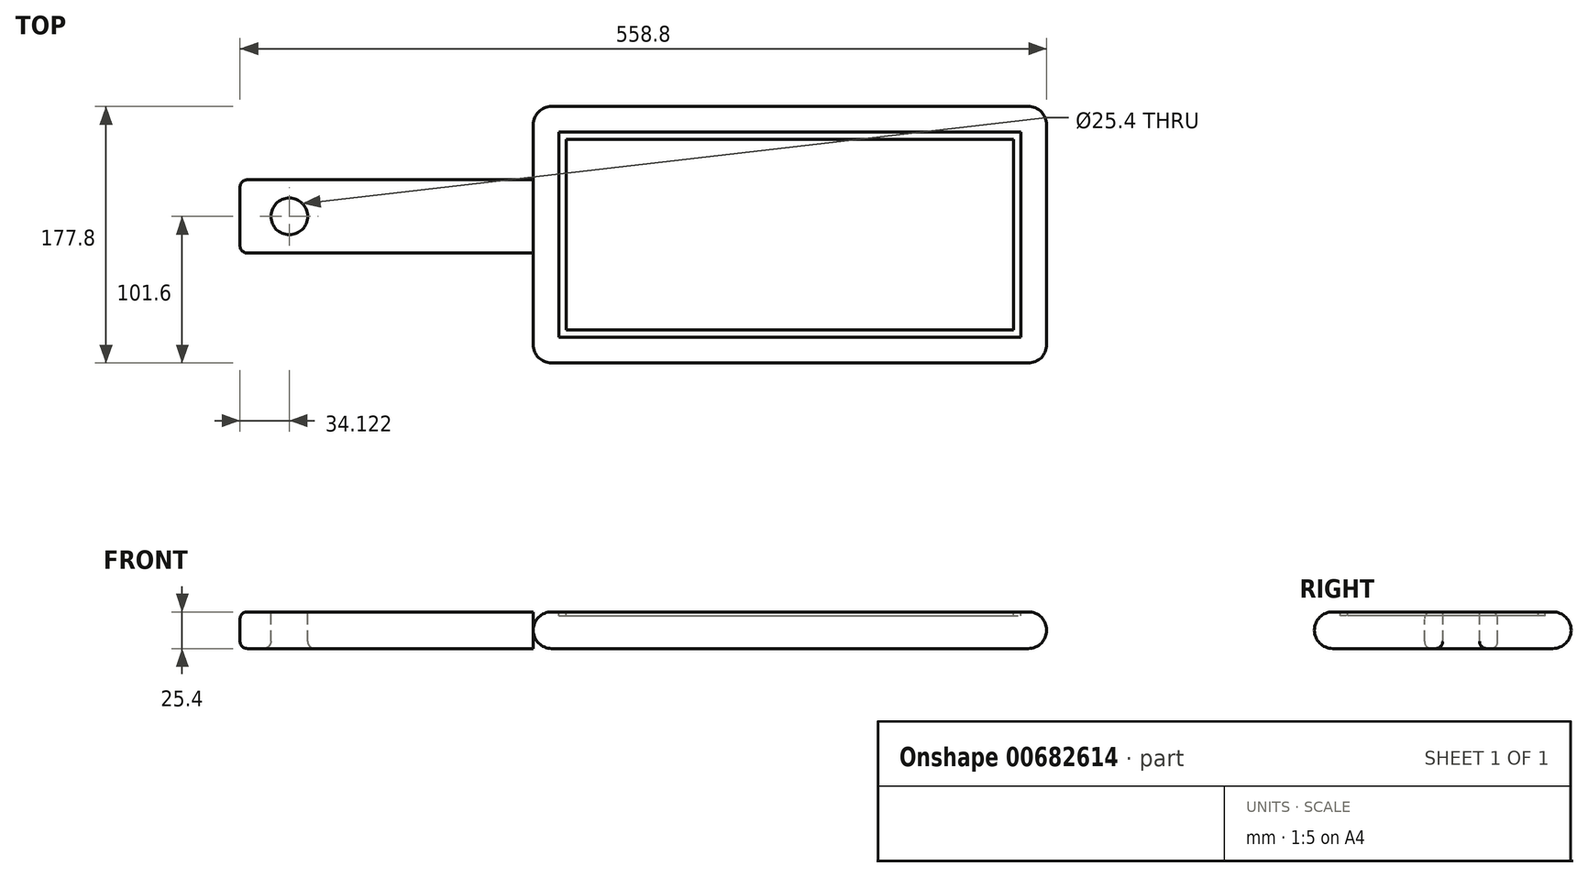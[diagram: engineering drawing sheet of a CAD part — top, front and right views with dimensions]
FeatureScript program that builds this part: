
annotation { "Feature Type Name" : "Feature", "Feature Type Description" : "" }
export const myFeature = defineFeature(function(context is Context, id is Id, definition is map)
    precondition{}
    {
        {
            var Q0;
            Q0=qCreatedBy(makeId("Top.planeOp"),FACE);
            var sketch = newSketch(context, id + "F0", { "sketchPlane" : qUnion([Q0])});
            skLineSegment(sketch, "E0.bottom", {"start": v(0, 0) * mm, "end": v(355.6, 0) * mm});
            skLineSegment(sketch, "E0.top", {"start": v(0, 177.8) * mm, "end": v(355.6, 177.8) * mm});
            skLineSegment(sketch, "E0.left", {"start": v(0, 0) * mm, "end": v(0, 177.8) * mm});
            skLineSegment(sketch, "E0.right", {"start": v(355.6, 0) * mm, "end": v(355.6, 177.8) * mm});
            skSolve(sketch);
        }
        {
            var Q0;
            Q0 = qSketchRegion(id + "F0", true);
            extrude(context, id + "F1", {"entities" : qUnion([Q0]), "depth" : 25.4 * mm, "offsetDistance" : 25.4 * mm});
        }
        {
            var Q0;
            Q0=makeQuery(id+"F1.opExtrude","CAP_FACE",FACE,{"disambiguationData":[OSD([sQuery(id+"F0.wireOp",EDGE,"E0.bottom"),sQuery(id+"F0.wireOp",EDGE,"E0.top"),sQuery(id+"F0.wireOp",EDGE,"E0.left"),sQuery(id+"F0.wireOp",EDGE,"E0.right")])],"isStart":false});
            var sketch = newSketch(context, id + "F2", { "sketchPlane" : qUnion([Q0])});
            skLineSegment(sketch, "E1.bottom", {"start": v(0, 127) * mm, "end": v(-203.2, 127) * mm});
            skLineSegment(sketch, "E1.top", {"start": v(0, 76.2) * mm, "end": v(-203.2, 76.2) * mm});
            skLineSegment(sketch, "E1.left", {"start": v(0, 127) * mm, "end": v(0, 76.2) * mm});
            skLineSegment(sketch, "E1.right", {"start": v(-203.2, 127) * mm, "end": v(-203.2, 76.2) * mm});
            skSolve(sketch);
        }
        {
            var Q0;
            Q0=makeQuery(id+"F2.imprint","IMPRINT",FACE,{"disambiguationData":[TD([[makeQuery(id+"F2.imprint","IMPRINT",EDGE,{"derivedFrom":sQuery(id+"F2.wireOp",EDGE,"E1.bottom")}),1.0]])]});
            extrude(context, id + "F3", {"entities" : qUnion([Q0]), "oppositeDirection" : true, "depth" : 25.4 * mm, "offsetDistance" : 25.4 * mm});
        }
        {
            var Q0;
            Q0=makeQuery(id+"F3.opExtrude","CAP_FACE",FACE,{"disambiguationData":[OSD([sQuery(id+"F2.wireOp",EDGE,"E1.bottom"),sQuery(id+"F2.wireOp",EDGE,"E1.top"),sQuery(id+"F2.wireOp",EDGE,"E1.left"),sQuery(id+"F2.wireOp",EDGE,"E1.right")])],"isStart":true});
            var sketch = newSketch(context, id + "F4", { "sketchPlane" : qUnion([Q0])});
            skCircle(sketch, "E2", {"center": v(-169.08, 101.6) * mm, "radius": 12.7 * mm});
            skSolve(sketch);
        }
        {
            var Q0;
            Q0=makeQuery(id+"F4.imprint","IMPRINT",FACE,{"disambiguationData":[TD([[makeQuery(id+"F4.imprint","IMPRINT",EDGE,{"derivedFrom":sQuery(id+"F4.wireOp",EDGE,"E2")}),1.0]])]});
            extrude(context, id + "F5", {"entities" : qUnion([Q0]), "operationType" : NewBodyOperationType.REMOVE, "endBound" : BoundingType.THROUGH_ALL, "oppositeDirection" : true, "depth" : 25.4 * mm, "offsetDistance" : 25.4 * mm});
        }
        {
            var Q0;
            Q0=makeQuery(id+"F5.boolean.opBoolean","COPY",EDGE,{"derivedFrom":makeQuery(id+"F5.opExtrude","CAP_EDGE",EDGE,{"disambiguationData":[OSD([sQuery(id+"F4.wireOp",EDGE,"E2")])],"isStart":true})});
            var Q1;
            Q1=makeQuery(id+"F5.boolean.opBoolean","INTERSECT",EDGE,{"derivedFrom":[makeQuery(id+"F3.opExtrude","CAP_FACE",FACE,{"disambiguationData":[OSD([sQuery(id+"F2.wireOp",EDGE,"E1.bottom"),sQuery(id+"F2.wireOp",EDGE,"E1.top"),sQuery(id+"F2.wireOp",EDGE,"E1.left"),sQuery(id+"F2.wireOp",EDGE,"E1.right")])],"isStart":false}),makeQuery(id+"F5.opExtrude","SWEPT_FACE",FACE,{"disambiguationData":[OSD([sQuery(id+"F4.wireOp",EDGE,"E2")])]})]});
            var Q2;
            Q2=makeQuery(id+"F3.opExtrude","CAP_EDGE",EDGE,{"disambiguationData":[OSD([sQuery(id+"F2.wireOp",EDGE,"E1.top")])],"isStart":false});
            var Q3;
            Q3=makeQuery(id+"F3.opExtrude","SWEPT_EDGE",EDGE,{"disambiguationData":[OSD([sQuery(id+"F2.wireOp",EDGE,"E1.top"),sQuery(id+"F2.wireOp",EDGE,"E1.right")])]});
            var Q4;
            Q4=makeQuery(id+"F3.opExtrude","CAP_EDGE",EDGE,{"disambiguationData":[OSD([sQuery(id+"F2.wireOp",EDGE,"E1.right")])],"isStart":false});
            var Q5;
            Q5=makeQuery(id+"F3.opExtrude","CAP_EDGE",EDGE,{"disambiguationData":[OSD([sQuery(id+"F2.wireOp",EDGE,"E1.right")])],"isStart":true});
            var Q6;
            Q6=makeQuery(id+"F3.opExtrude","CAP_EDGE",EDGE,{"disambiguationData":[OSD([sQuery(id+"F2.wireOp",EDGE,"E1.bottom")])],"isStart":true});
            var Q7;
            Q7=makeQuery(id+"F3.opExtrude","SWEPT_EDGE",EDGE,{"disambiguationData":[OSD([sQuery(id+"F2.wireOp",EDGE,"E1.bottom"),sQuery(id+"F2.wireOp",EDGE,"E1.right")])]});
            var Q8;
            Q8=makeQuery(id+"F3.opExtrude","CAP_EDGE",EDGE,{"disambiguationData":[OSD([sQuery(id+"F2.wireOp",EDGE,"E1.bottom")])],"isStart":false});
            var Q9;
            Q9=makeQuery(id+"F3.opExtrude","CAP_EDGE",EDGE,{"disambiguationData":[OSD([sQuery(id+"F2.wireOp",EDGE,"E1.top")])],"isStart":true});
            fillet(context, id + "F6", {"entities" : qUnion([Q0, Q1, Q2, Q3, Q4, Q5, Q6, Q7, Q8, Q9]), "radius" : 5.08 * mm, "tangentPropagation" : true, "allowEdgeOverflow" : false});
        }
        {
            var Q0;
            Q0=makeQuery(id+"F1.opExtrude","CAP_EDGE",EDGE,{"disambiguationData":[OSD([sQuery(id+"F0.wireOp",EDGE,"E0.left")])],"isStart":false});
            var Q1;
            Q1=makeQuery(id+"F1.opExtrude","CAP_EDGE",EDGE,{"disambiguationData":[OSD([sQuery(id+"F0.wireOp",EDGE,"E0.left")])],"isStart":true});
            var Q2;
            Q2=makeQuery(id+"F1.opExtrude","SWEPT_EDGE",EDGE,{"disambiguationData":[OSD([sQuery(id+"F0.wireOp",EDGE,"E0.top"),sQuery(id+"F0.wireOp",EDGE,"E0.left")])]});
            var Q3;
            Q3=makeQuery(id+"F1.opExtrude","CAP_EDGE",EDGE,{"disambiguationData":[OSD([sQuery(id+"F0.wireOp",EDGE,"E0.top")])],"isStart":false});
            var Q4;
            Q4=makeQuery(id+"F1.opExtrude","SWEPT_EDGE",EDGE,{"disambiguationData":[OSD([sQuery(id+"F0.wireOp",EDGE,"E0.top"),sQuery(id+"F0.wireOp",EDGE,"E0.right")])]});
            var Q5;
            Q5=makeQuery(id+"F1.opExtrude","CAP_EDGE",EDGE,{"disambiguationData":[OSD([sQuery(id+"F0.wireOp",EDGE,"E0.right")])],"isStart":true});
            var Q6;
            Q6=makeQuery(id+"F1.opExtrude","CAP_EDGE",EDGE,{"disambiguationData":[OSD([sQuery(id+"F0.wireOp",EDGE,"E0.right")])],"isStart":false});
            var Q7;
            Q7=makeQuery(id+"F1.opExtrude","SWEPT_FACE",FACE,{"disambiguationData":[OSD([sQuery(id+"F0.wireOp",EDGE,"E0.bottom")])]});
            var Q8;
            Q8=makeQuery(id+"F1.opExtrude","CAP_EDGE",EDGE,{"disambiguationData":[OSD([sQuery(id+"F0.wireOp",EDGE,"E0.top")])],"isStart":true});
            fillet(context, id + "F7", {"entities" : qUnion([Q0, Q1, Q2, Q3, Q4, Q5, Q6, Q7, Q8]), "radius" : 12.7 * mm, "tangentPropagation" : true, "allowEdgeOverflow" : false});
        }
        {
            var Q0;
            Q0=makeQuery(id+"F1.opExtrude","CAP_FACE",FACE,{"disambiguationData":[OSD([sQuery(id+"F0.wireOp",EDGE,"E0.bottom"),sQuery(id+"F0.wireOp",EDGE,"E0.top"),sQuery(id+"F0.wireOp",EDGE,"E0.left"),sQuery(id+"F0.wireOp",EDGE,"E0.right")])],"isStart":false});
            var sketch = newSketch(context, id + "F8", { "sketchPlane" : qUnion([Q0])});
            skLineSegment(sketch, "E3.bottom", {"start": v(17.78, 160.02) * mm, "end": v(337.82, 160.02) * mm});
            skLineSegment(sketch, "E3.top", {"start": v(17.78, 17.78) * mm, "end": v(337.82, 17.78) * mm});
            skLineSegment(sketch, "E3.left", {"start": v(17.78, 160.02) * mm, "end": v(17.78, 17.78) * mm});
            skLineSegment(sketch, "E3.right", {"start": v(337.82, 160.02) * mm, "end": v(337.82, 17.78) * mm});
            skLineSegment(sketch, "E4.bottom", {"start": v(22.86, 154.94) * mm, "end": v(332.74, 154.94) * mm});
            skLineSegment(sketch, "E4.top", {"start": v(22.86, 22.86) * mm, "end": v(332.74, 22.86) * mm});
            skLineSegment(sketch, "E4.left", {"start": v(22.86, 154.94) * mm, "end": v(22.86, 22.86) * mm});
            skLineSegment(sketch, "E4.right", {"start": v(332.74, 154.94) * mm, "end": v(332.74, 22.86) * mm});
            skSolve(sketch);
        }
        {
            var Q0;
            Q0=makeQuery(id+"F8.imprint","IMPRINT",FACE,{"disambiguationData":[TD([[makeQuery(id+"F8.imprint","IMPRINT",EDGE,{"derivedFrom":sQuery(id+"F8.wireOp",EDGE,"E3.bottom")}),-1.0]])]});
            extrude(context, id + "F9", {"entities" : qUnion([Q0]), "operationType" : NewBodyOperationType.REMOVE, "oppositeDirection" : true, "depth" : 2.54 * mm, "offsetDistance" : 25.4 * mm});
        }
    });
